# Revit family: Mirror_Metlam_Polished
name_source: partatom
category: Specialty Equipment
revit_build: Autodesk Revit 2016 (Build: 20170117_1200(x64)
units: mm (PartAtom-declared; Revit-internal decimal feet)

## family parameters
Always vertical = Yes
Cut with Voids When Loaded = No
OmniClass Number = 23.40.95.17.17
OmniClass Title = Mirrors
Part Type = Normal
Room Calculation Point = Yes
Round Connector Dimension = Use Diameter
Shared = No
Work Plane-Based = No

## types (1)
- 500w x 8d x 950h (ML777)
    Description = Stainless Steel Polished Mirror
    Manufacturer = Metlam
    Manufacturer_Overall Depth = 8 mm  [stored 0.0262467 ft]
    Manufacturer_Overall Height = 950 mm  [stored 3.1168 ft]
    Manufacturer_Overall Width = 500 mm  [stored 1.64042 ft]
    Manufacturer_Spec Code = ML777
    Manufacturer_URL__Product Specific = https://metlam.com.au
    Material_ANZRS = z_Metlam_Metal_Stainless Steel_Polished
    Model = ML777
    Type Comments = Mirrors
    URL = http://www.metlam.com.au

note: [stored X ft] marks values corroborated as IEEE doubles in the binary element streams (Revit-internal decimal feet)

## geometry (parser evidence)
native form markers: Sweep x3
no freeform markers — native parametric forms only
